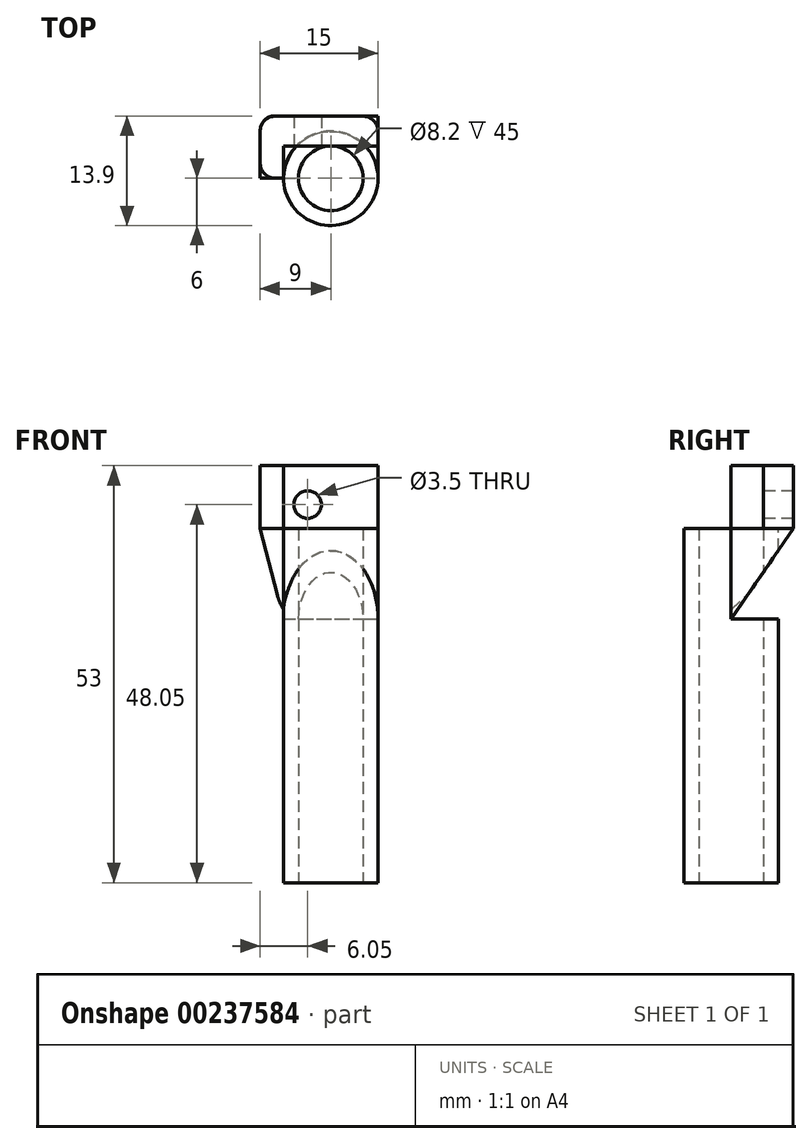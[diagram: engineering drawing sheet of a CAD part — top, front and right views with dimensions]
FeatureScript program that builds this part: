
annotation { "Feature Type Name" : "Feature", "Feature Type Description" : "" }
export const myFeature = defineFeature(function(context is Context, id is Id, definition is map)
    precondition{}
    {
        {
            var Q0;
            Q0=qCreatedBy(makeId("Top.planeOp"),FACE);
            var sketch = newSketch(context, id + "F0", { "sketchPlane" : qUnion([Q0])});
            skCircle(sketch, "E0", {"center": v(0, 0) * mm, "radius": 4.1 * mm});
            skCircle(sketch, "E1", {"center": v(0, 0) * mm, "radius": 6 * mm});
            skSolve(sketch);
        }
        {
            var Q0;
            Q0=makeQuery(id+"F0.imprint","IMPRINT",FACE,{"disambiguationData":[TD([[makeQuery(id+"F0.imprint","IMPRINT",EDGE,{"derivedFrom":sQuery(id+"F0.wireOp",EDGE,"E0")}),-1.0]])]});
            extrude(context, id + "F1", {"entities" : qUnion([Q0]), "depth" : 45 * mm});
        }
        {
            var Q0;
            Q0=makeQuery(id+"F1.opExtrude","CAP_FACE",FACE,{"disambiguationData":[OSD([sQuery(id+"F0.wireOp",EDGE,"E0"),sQuery(id+"F0.wireOp",EDGE,"E1")])],"isStart":false});
            var sketch = newSketch(context, id + "F2", { "sketchPlane" : qUnion([Q0])});
            skCircle(sketch, "E2.0", {"center": v(0, 0) * mm, "radius": 4.1 * mm});
            skSolve(sketch);
        }
        {
            var Q0;
            Q0=makeQuery(id+"F2.imprint","IMPRINT",FACE,{"disambiguationData":[TD([[makeQuery(id+"F2.imprint","IMPRINT",EDGE,{"derivedFrom":sQuery(id+"F2.wireOp",EDGE,"E2.0")}),-1.0]])]});
            var sketch = newSketch(context, id + "F3", { "sketchPlane" : qUnion([Q0])});
            skCircle(sketch, "E3.0", {"center": v(0, 0) * mm, "radius": 4.1 * mm});
            skPoint(sketch, "E4", {"position": v(-6, 0) * mm});
            skPoint(sketch, "E5", {"position": v(4.1, 0) * mm});
            skPoint(sketch, "E6", {"position": v(0, 4.1) * mm});
            skPoint(sketch, "E7", {"position": v(0, -4.1) * mm});
            skLineSegment(sketch, "E8.top", {"start": v(6, 7.9) * mm, "end": v(-9, 7.9) * mm});
            skLineSegment(sketch, "E8.left", {"start": v(6, 0) * mm, "end": v(6, 7.9) * mm});
            skLineSegment(sketch, "E8.right", {"start": v(-9, 0) * mm, "end": v(-9, 7.9) * mm});
            skLineSegment(sketch, "E9.bottom", {"start": v(-6, 4.1) * mm, "end": v(23.9, 4.1) * mm});
            skLineSegment(sketch, "E9.top", {"start": v(-6, -5.9) * mm, "end": v(23.9, -5.9) * mm});
            skLineSegment(sketch, "E9.right", {"start": v(23.9, 4.1) * mm, "end": v(23.9, -5.9) * mm});
            skLineSegment(sketch, "E10", {"start": v(-9, 0) * mm, "end": v(-6, 0) * mm});
            skLineSegment(sketch, "E11", {"start": v(-6, 4.1) * mm, "end": v(-6, -5.9) * mm});
            skCircle(sketch, "E12.0", {"center": v(0, 0) * mm, "radius": 6 * mm});
            skPoint(sketch, "E13", {"position": v(-4.38, 4.1) * mm});
            skPoint(sketch, "E14", {"position": v(4.38, 4.1) * mm});
            skSolve(sketch);
        }
        {
            var Q0;
            {var subQ0=sQuery(id+"F3.wireOp",EDGE,"E8.top");Q0=makeQuery(id+"F3.imprint","IMPRINT",FACE,{"disambiguationData":[TD([[makeQuery(id+"F3.imprint","IMPRINT",EDGE,{"derivedFrom":subQ0}),1.0]])]});}
            var Q1;
            {var subQ0=sQuery(id+"F3.wireOp",EDGE,"E11");var subQ1=sQuery(id+"F3.wireOp",EDGE,"E9.bottom");var subQ2=makeQuery(id+"F3.imprint","INTERSECT",VERTEX,{"derivedFrom":[subQ1,subQ0]});Q1=makeQuery(id+"F3.imprint","IMPRINT",FACE,{"disambiguationData":[TD([[makeQuery(id+"F3.imprint","IMPRINT",EDGE,{"disambiguationData":[TD([[subQ2,-1.0]])],"derivedFrom":subQ1}),-1.0]])]});}
            var Q2;
            {var subQ0=sQuery(id+"F3.wireOp",EDGE,"E12.0");var subQ1=sQuery(id+"F3.wireOp",EDGE,"E8.left");var subQ2=makeQuery(id+"F3.imprint","INTERSECT",VERTEX,{"derivedFrom":[subQ1,subQ0]});Q2=makeQuery(id+"F3.imprint","IMPRINT",FACE,{"disambiguationData":[TD([[makeQuery(id+"F3.imprint","IMPRINT",EDGE,{"disambiguationData":[TD([[subQ2,-1.0]])],"derivedFrom":subQ1}),1.0]])]});}
            extrude(context, id + "F4", {"entities" : qUnion([Q0, Q1, Q2]), "oppositeDirection" : true, "depth" : 11.5 * mm});
        }
        {
            var Q0;
            {var subQ0=sQuery(id+"F3.wireOp",EDGE,"E8.top");Q0=makeQuery(id+"F3.imprint","IMPRINT",FACE,{"disambiguationData":[TD([[makeQuery(id+"F3.imprint","IMPRINT",EDGE,{"derivedFrom":subQ0}),1.0]])]});}
            var Q1;
            {var subQ0=sQuery(id+"F3.wireOp",EDGE,"E9.bottom");var subQ1=makeQuery(id+"F3.imprint","INTERSECT",VERTEX,{"derivedFrom":[sQuery(id+"F3.wireOp",EDGE,"E3.0"),subQ0]});Q1=makeQuery(id+"F3.imprint","IMPRINT",FACE,{"disambiguationData":[TD([[makeQuery(id+"F3.imprint","IMPRINT",EDGE,{"disambiguationData":[TD([[subQ1,1.0]])],"derivedFrom":subQ0}),1.0]])]});}
            extrude(context, id + "F5", {"entities" : qUnion([Q0, Q1]), "depth" : 8 * mm});
        }
        {
            var Q0;
            Q0=makeQuery(id+"F5.opExtrude","SWEPT_FACE",FACE,{"disambiguationData":[OSD([sQuery(id+"F3.wireOp",EDGE,"E9.bottom")])]});
            var sketch = newSketch(context, id + "F6", { "sketchPlane" : qUnion([Q0])});
            skCircle(sketch, "E15", {"center": v(-2.95, 48.05) * mm, "radius": 1.75 * mm});
            skSolve(sketch);
        }
        {
            var Q0;
            Q0=makeQuery(id+"F6.imprint","IMPRINT",FACE,{"disambiguationData":[TD([[makeQuery(id+"F6.imprint","IMPRINT",EDGE,{"derivedFrom":sQuery(id+"F6.wireOp",EDGE,"E15")}),1.0]])]});
            extrude(context, id + "F7", {"entities" : qUnion([Q0]), "operationType" : NewBodyOperationType.REMOVE, "oppositeDirection" : true, "depth" : 25 * mm});
        }
        {
            var Q0;
            Q0=makeQuery(id+"F4.opExtrude","SWEPT_FACE",FACE,{"disambiguationData":[OSD([sQuery(id+"F3.wireOp",EDGE,"E10")])]});
            var sketch = newSketch(context, id + "F8", { "sketchPlane" : qUnion([Q0])});
            skLineSegment(sketch, "E16", {"start": v(-9, 45) * mm, "end": v(-6, 33.5) * mm});
            skLineSegment(sketch, "E17", {"start": v(-6, 33.5) * mm, "end": v(-9, 33.5) * mm});
            skLineSegment(sketch, "E18", {"start": v(-9, 33.5) * mm, "end": v(-9, 45) * mm});
            skSolve(sketch);
        }
        {
            var Q0;
            Q0=makeQuery(id+"F8.imprint","IMPRINT",FACE,{"disambiguationData":[TD([[makeQuery(id+"F8.imprint","IMPRINT",EDGE,{"derivedFrom":sQuery(id+"F8.wireOp",EDGE,"E16")}),-1.0]])]});
            extrude(context, id + "F9", {"entities" : qUnion([Q0]), "operationType" : NewBodyOperationType.REMOVE, "oppositeDirection" : true, "depth" : 50 * mm});
        }
        {
            var Q0;
            Q0=makeQuery(id+"F4.opExtrude","SWEPT_FACE",FACE,{"disambiguationData":[OSD([sQuery(id+"F3.wireOp",EDGE,"E8.left")])]});
            var sketch = newSketch(context, id + "F10", { "sketchPlane" : qUnion([Q0])});
            skLineSegment(sketch, "E19", {"start": v(0, 33.5) * mm, "end": v(7.9, 45) * mm});
            skLineSegment(sketch, "E20", {"start": v(7.9, 45) * mm, "end": v(7.9, 33.5) * mm});
            skLineSegment(sketch, "E21", {"start": v(7.9, 33.5) * mm, "end": v(0, 33.5) * mm});
            skSolve(sketch);
        }
        {
            var Q0;
            Q0=makeQuery(id+"F10.imprint","IMPRINT",FACE,{"disambiguationData":[TD([[makeQuery(id+"F10.imprint","IMPRINT",EDGE,{"derivedFrom":sQuery(id+"F10.wireOp",EDGE,"E19")}),-1.0]])]});
            extrude(context, id + "F11", {"entities" : qUnion([Q0]), "operationType" : NewBodyOperationType.REMOVE, "oppositeDirection" : true, "depth" : 25 * mm});
        }
        {
            var Q0;
            Q0=makeQuery(id+"F5.opExtrude","SWEPT_EDGE",EDGE,{"disambiguationData":[OSD([sQuery(id+"F3.wireOp",EDGE,"E8.right"),sQuery(id+"F3.wireOp",EDGE,"E10")])]});
            var Q1;
            Q1=makeQuery(id+"F9.boolean.opBoolean","COPY",EDGE,{"derivedFrom":makeQuery(id+"F9.opExtrude","CAP_EDGE",EDGE,{"disambiguationData":[OSD([sQuery(id+"F8.wireOp",EDGE,"E16")])],"isStart":true})});
            var Q2;
            Q2=makeQuery(id+"F5.opExtrude","SWEPT_EDGE",EDGE,{"disambiguationData":[OSD([sQuery(id+"F3.wireOp",EDGE,"E8.top"),sQuery(id+"F3.wireOp",EDGE,"E8.right")])]});
            var Q3;
            Q3=makeQuery(id+"F11.boolean.opBoolean","INTERSECT",EDGE,{"derivedFrom":[makeQuery(id+"F9.boolean.opBoolean","COPY",FACE,{"derivedFrom":makeQuery(id+"F9.opExtrude","SWEPT_FACE",FACE,{"disambiguationData":[OSD([sQuery(id+"F8.wireOp",EDGE,"E16")])]})}),makeQuery(id+"F11.opExtrude","SWEPT_FACE",FACE,{"disambiguationData":[OSD([sQuery(id+"F10.wireOp",EDGE,"E19")])]})]});
            var Q4;
            Q4=makeQuery(id+"F5.opExtrude","SWEPT_EDGE",EDGE,{"disambiguationData":[OSD([sQuery(id+"F3.wireOp",EDGE,"E8.top"),sQuery(id+"F3.wireOp",EDGE,"E8.left")])]});
            var Q5;
            Q5=makeQuery(id+"F11.boolean.opBoolean","COPY",EDGE,{"derivedFrom":makeQuery(id+"F11.opExtrude","CAP_EDGE",EDGE,{"disambiguationData":[OSD([sQuery(id+"F10.wireOp",EDGE,"E19")])],"isStart":true})});
            fillet(context, id + "F12", {"entities" : qUnion([Q0, Q1, Q2, Q3, Q4, Q5]), "radius" : 2 * mm, "tangentPropagation" : true, "allowEdgeOverflow" : false});
        }
    });
